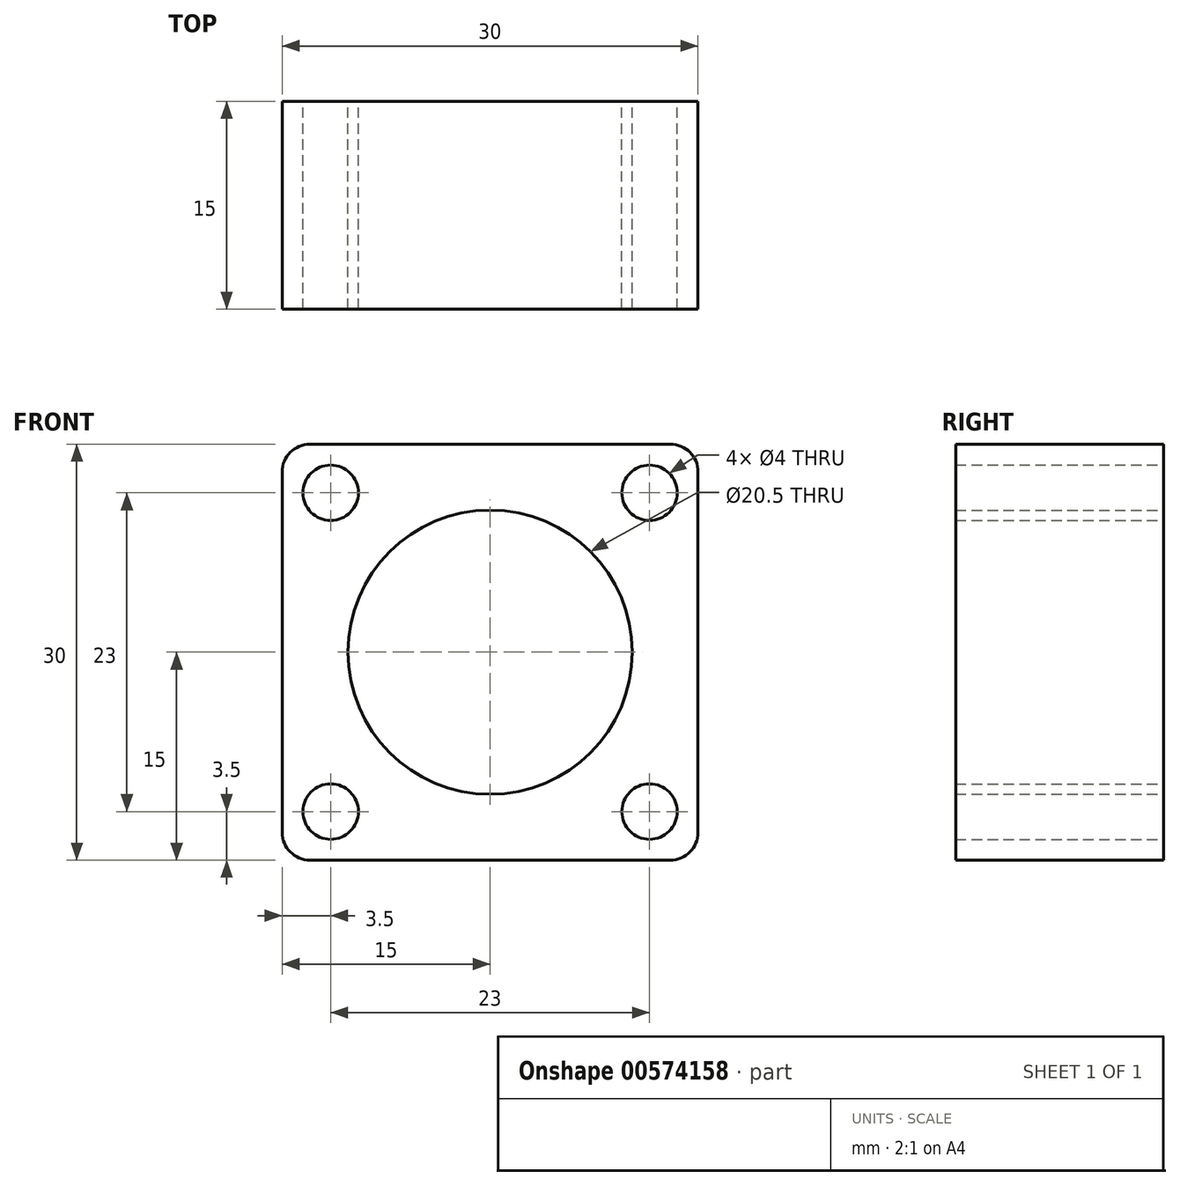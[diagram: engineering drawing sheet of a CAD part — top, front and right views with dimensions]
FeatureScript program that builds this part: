
annotation { "Feature Type Name" : "Feature", "Feature Type Description" : "" }
export const myFeature = defineFeature(function(context is Context, id is Id, definition is map)
    precondition{}
    {
        {
            var Q0;
            Q0=qCreatedBy(makeId("Front.planeOp"),FACE);
            var sketch = newSketch(context, id + "F0", { "sketchPlane" : qUnion([Q0])});
            skLineSegment(sketch, "E0.bottom", {"start": v(-13, 15) * mm, "end": v(13, 15) * mm});
            skLineSegment(sketch, "E0.top", {"start": v(-13, -15) * mm, "end": v(13, -15) * mm});
            skLineSegment(sketch, "E0.left", {"start": v(-15, 13) * mm, "end": v(-15, -13) * mm});
            skLineSegment(sketch, "E0.right", {"start": v(15, 13) * mm, "end": v(15, -13) * mm});
            skCircle(sketch, "E1", {"center": v(0, 0) * mm, "radius": 10.25 * mm});
            skPoint(sketch, "E2.visualSharp", {"position": v(-15, 15) * mm});
            skArc(sketch, "E2.filletArc", {"start": v(-13, 15) * mm, "mid": v(-14.41, 14.41) * mm, "end": v(-15, 13) * mm});
            skPoint(sketch, "E3.visualSharp", {"position": v(15, 15) * mm});
            skArc(sketch, "E3.filletArc", {"start": v(15, 13) * mm, "mid": v(14.41, 14.41) * mm, "end": v(13, 15) * mm});
            skPoint(sketch, "E4.visualSharp", {"position": v(15, -15) * mm});
            skArc(sketch, "E4.filletArc", {"start": v(13, -15) * mm, "mid": v(14.41, -14.41) * mm, "end": v(15, -13) * mm});
            skPoint(sketch, "E5.visualSharp", {"position": v(-15, -15) * mm});
            skArc(sketch, "E5.filletArc", {"start": v(-15, -13) * mm, "mid": v(-14.41, -14.41) * mm, "end": v(-13, -15) * mm});
            skCircle(sketch, "E6", {"center": v(-11.5, 11.5) * mm, "radius": 2 * mm});
            skCircle(sketch, "E7.0.1.0", {"center": v(-11.5, -11.5) * mm, "radius": 2 * mm});
            skCircle(sketch, "E7.1.0.0", {"center": v(11.5, 11.5) * mm, "radius": 2 * mm});
            skCircle(sketch, "E7.1.1.0", {"center": v(11.5, -11.5) * mm, "radius": 2 * mm});
            skLineSegment(sketch, "E7.direction1", {"start": v(-11.5, 11.5) * mm, "end": v(11.5, 11.5) * mm, "construction": true});
            skLineSegment(sketch, "E7.direction2", {"start": v(-11.5, 11.5) * mm, "end": v(-11.5, -11.5) * mm, "construction": true});
            skSolve(sketch);
        }
        {
            var Q0;
            Q0=makeQuery(id+"F0.imprint","IMPRINT",FACE,{"disambiguationData":[TD([[makeQuery(id+"F0.imprint","IMPRINT",EDGE,{"derivedFrom":sQuery(id+"F0.wireOp",EDGE,"E0.bottom")}),-1.0]])]});
            extrude(context, id + "F1", {"entities" : qUnion([Q0]), "depth" : 15 * mm, "offsetDistance" : 25 * mm});
        }
    });
